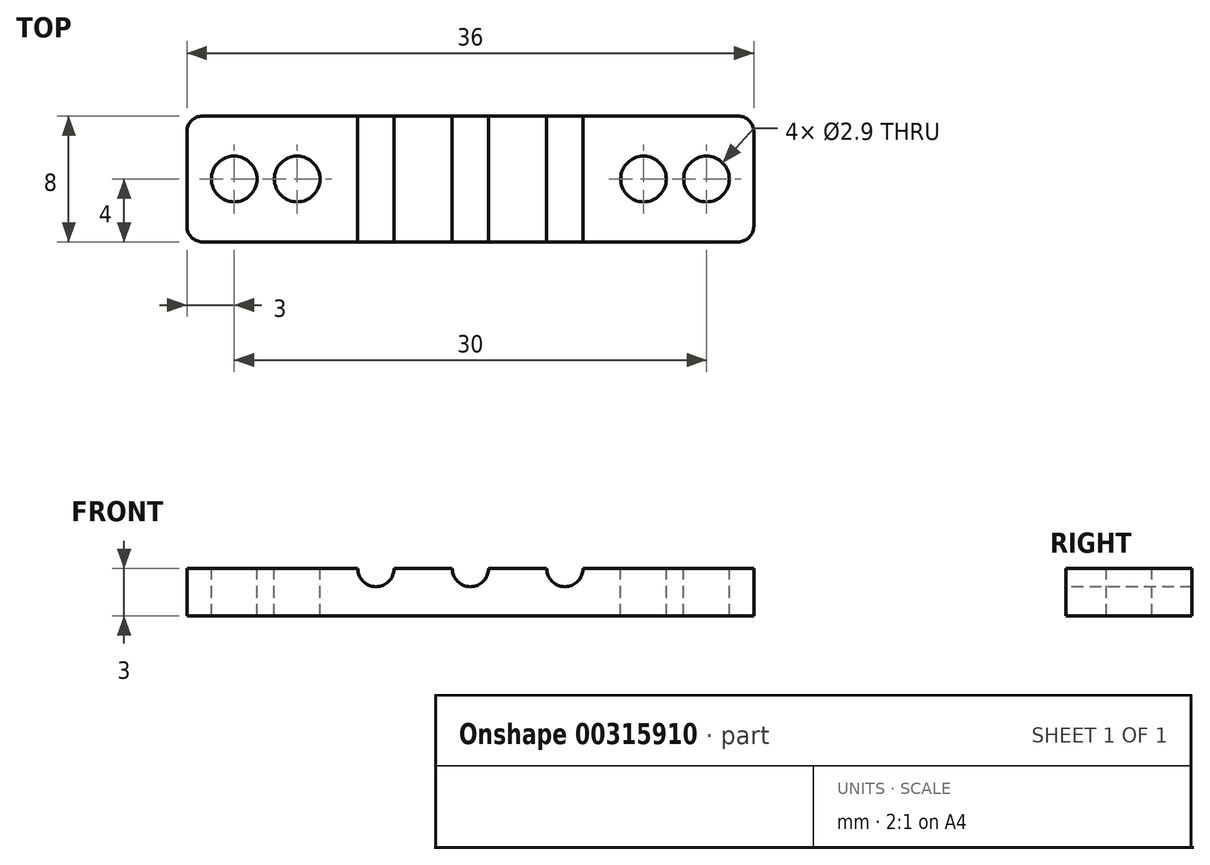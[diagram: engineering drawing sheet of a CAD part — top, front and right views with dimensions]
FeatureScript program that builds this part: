
annotation { "Feature Type Name" : "Feature", "Feature Type Description" : "" }
export const myFeature = defineFeature(function(context is Context, id is Id, definition is map)
    precondition{}
    {
        {
            var Q0;
            Q0=qCreatedBy(makeId("Top.planeOp"),FACE);
            var sketch = newSketch(context, id + "F0", { "sketchPlane" : qUnion([Q0])});
            skLineSegment(sketch, "E0.bottom", {"start": v(3, 4) * mm, "end": v(-3, 4) * mm});
            skLineSegment(sketch, "E0.top", {"start": v(3, -4) * mm, "end": v(-3, -4) * mm});
            skLineSegment(sketch, "E0.left", {"start": v(3, 4) * mm, "end": v(3, -4) * mm});
            skLineSegment(sketch, "E0.right", {"start": v(-3, 4) * mm, "end": v(-3, -4) * mm});
            skPoint(sketch, "E0.middle", {"position": v(0, 0) * mm});
            skLineSegment(sketch, "E1.bottom", {"start": v(33, 4) * mm, "end": v(27, 4) * mm});
            skLineSegment(sketch, "E1.top", {"start": v(33, -4) * mm, "end": v(27, -4) * mm});
            skLineSegment(sketch, "E1.left", {"start": v(33, 4) * mm, "end": v(33, -4) * mm});
            skLineSegment(sketch, "E1.right", {"start": v(27, 4) * mm, "end": v(27, -4) * mm});
            skPoint(sketch, "E1.middle", {"position": v(30, 0) * mm});
            skLineSegment(sketch, "E2", {"start": v(3, 4) * mm, "end": v(27, 4) * mm});
            skLineSegment(sketch, "E3", {"start": v(3, -4) * mm, "end": v(27, -4) * mm});
            skLineSegment(sketch, "E4", {"start": v(9, 4) * mm, "end": v(9, -4) * mm, "construction": true});
            skLineSegment(sketch, "E5.1.0.0", {"start": v(15, 4) * mm, "end": v(15, -4) * mm, "construction": true});
            skLineSegment(sketch, "E5.2.0.0", {"start": v(21, 4) * mm, "end": v(21, -4) * mm, "construction": true});
            skLineSegment(sketch, "E5.direction1", {"start": v(9, -4) * mm, "end": v(15, -4) * mm, "construction": true});
            skPoint(sketch, "E6", {"position": v(4, 0) * mm});
            skPoint(sketch, "E6.positionSnap0", {"position": v(3, 0) * mm});
            skPoint(sketch, "E7", {"position": v(26, 0) * mm});
            skPoint(sketch, "E7.positionSnap0", {"position": v(27, 0) * mm});
            skSolve(sketch);
        }
        {
            var Q0;
            Q0=makeQuery(id+"F0.imprint","IMPRINT",FACE,{"disambiguationData":[TD([[makeQuery(id+"F0.imprint","IMPRINT",EDGE,{"derivedFrom":sQuery(id+"F0.wireOp",EDGE,"E0.bottom")}),1.0]])]});
            var Q1;
            Q1=makeQuery(id+"F0.imprint","IMPRINT",FACE,{"disambiguationData":[TD([[makeQuery(id+"F0.imprint","IMPRINT",EDGE,{"derivedFrom":sQuery(id+"F0.wireOp",EDGE,"E0.left")}),1.0]])]});
            var Q2;
            Q2=makeQuery(id+"F0.imprint","IMPRINT",FACE,{"disambiguationData":[TD([[makeQuery(id+"F0.imprint","IMPRINT",EDGE,{"derivedFrom":sQuery(id+"F0.wireOp",EDGE,"E1.bottom")}),1.0]])]});
            extrude(context, id + "F1", {"entities" : qUnion([Q0, Q1, Q2]), "oppositeDirection" : true, "depth" : 3 * mm});
        }
        {
            var Q0;
            Q0=sQuery(id+"F0.wireOp",VERTEX,"E0.middle");
            var Q1;
            Q1=sQuery(id+"F0.wireOp",VERTEX,"E6");
            var Q2;
            Q2=sQuery(id+"F0.wireOp",VERTEX,"E7");
            var Q3;
            Q3=sQuery(id+"F0.wireOp",VERTEX,"E1.middle");
            var Q4;
            Q4=makeQuery(id+"F1.opExtrude","SWEPT_BODY",BODY,{"disambiguationData":[OSD([sQuery(id+"F0.wireOp",EDGE,"E0.bottom"),sQuery(id+"F0.wireOp",EDGE,"E0.top"),sQuery(id+"F0.wireOp",EDGE,"E0.right"),sQuery(id+"F0.wireOp",EDGE,"E1.bottom"),sQuery(id+"F0.wireOp",EDGE,"E1.top"),sQuery(id+"F0.wireOp",EDGE,"E1.left"),sQuery(id+"F0.wireOp",EDGE,"E2"),sQuery(id+"F0.wireOp",EDGE,"E3")])]});
            hole(context, id + "F2", {"style" : HoleStyle.SIMPLE, "endStyle" : HoleEndStyle.THROUGH, "holeDiameter" : 2.9 * mm, "tappedDepth" : 12 * mm, "tapClearance" : 3, "locations" : qUnion([Q0, Q1, Q2, Q3]), "scope" : qUnion([Q4])});
        }
        {
            var Q0;
            {var subQ0=sQuery(id+"F0.wireOp",EDGE,"E3");var subQ1=sQuery(id+"F0.wireOp",EDGE,"E1.top");var subQ2=sQuery(id+"F0.wireOp",EDGE,"E0.top");Q0=makeQuery(id+"FaaVOSY5iOmgxNq_1.boolean.opBoolean","MERGE",FACE,{"derivedFrom":[makeQuery(id+"F1.opExtrude","SWEPT_FACE",FACE,{"disambiguationData":[OSD([subQ2,subQ1,subQ0])]}),makeQuery(id+"FaaVOSY5iOmgxNq_1.opExtrude","SWEPT_FACE",FACE,{"disambiguationData":[OSD([subQ2,subQ1,subQ0])]})]});}
            var sketch = newSketch(context, id + "F3", { "sketchPlane" : qUnion([Q0])});
            skPoint(sketch, "E8", {"position": v(9, 0) * mm});
            skPoint(sketch, "E9", {"position": v(15, 0) * mm});
            skPoint(sketch, "E10", {"position": v(21, 0) * mm});
            skSolve(sketch);
        }
        {
            var Q0;
            Q0=sQuery(id+"F3.wireOp",VERTEX,"E8");
            var Q1;
            Q1=sQuery(id+"F3.wireOp",VERTEX,"E10");
            var Q2;
            Q2=sQuery(id+"F3.wireOp",VERTEX,"E9");
            var Q3;
            Q3=makeQuery(id+"F1.opExtrude","SWEPT_BODY",BODY,{"disambiguationData":[OSD([sQuery(id+"F0.wireOp",EDGE,"E0.bottom"),sQuery(id+"F0.wireOp",EDGE,"E0.top"),sQuery(id+"F0.wireOp",EDGE,"E0.right"),sQuery(id+"F0.wireOp",EDGE,"E1.bottom"),sQuery(id+"F0.wireOp",EDGE,"E1.top"),sQuery(id+"F0.wireOp",EDGE,"E1.left"),sQuery(id+"F0.wireOp",EDGE,"E2"),sQuery(id+"F0.wireOp",EDGE,"E3")])]});
            hole(context, id + "F4", {"style" : HoleStyle.SIMPLE, "endStyle" : HoleEndStyle.THROUGH, "holeDiameter" : 2.3 * mm, "tappedDepth" : 12 * mm, "tapClearance" : 3, "locations" : qUnion([Q0, Q1, Q2]), "scope" : qUnion([Q3])});
        }
        {
            var Q0;
            Q0=makeQuery(id+"F1.opExtrude","SWEPT_EDGE",EDGE,{"disambiguationData":[OSD([sQuery(id+"F0.wireOp",EDGE,"E0.top"),sQuery(id+"F0.wireOp",EDGE,"E0.right")])]});
            var Q1;
            Q1=makeQuery(id+"F1.opExtrude","SWEPT_EDGE",EDGE,{"disambiguationData":[OSD([sQuery(id+"F0.wireOp",EDGE,"E1.top"),sQuery(id+"F0.wireOp",EDGE,"E1.left")])]});
            var Q2;
            Q2=makeQuery(id+"F1.opExtrude","SWEPT_EDGE",EDGE,{"disambiguationData":[OSD([sQuery(id+"F0.wireOp",EDGE,"E1.bottom"),sQuery(id+"F0.wireOp",EDGE,"E1.left")])]});
            var Q3;
            Q3=makeQuery(id+"F1.opExtrude","SWEPT_EDGE",EDGE,{"disambiguationData":[OSD([sQuery(id+"F0.wireOp",EDGE,"E0.bottom"),sQuery(id+"F0.wireOp",EDGE,"E0.right")])]});
            fillet(context, id + "F5", {"entities" : qUnion([Q0, Q1, Q2, Q3]), "radius" : 1 * mm, "tangentPropagation" : true, "allowEdgeOverflow" : false});
        }
    });
